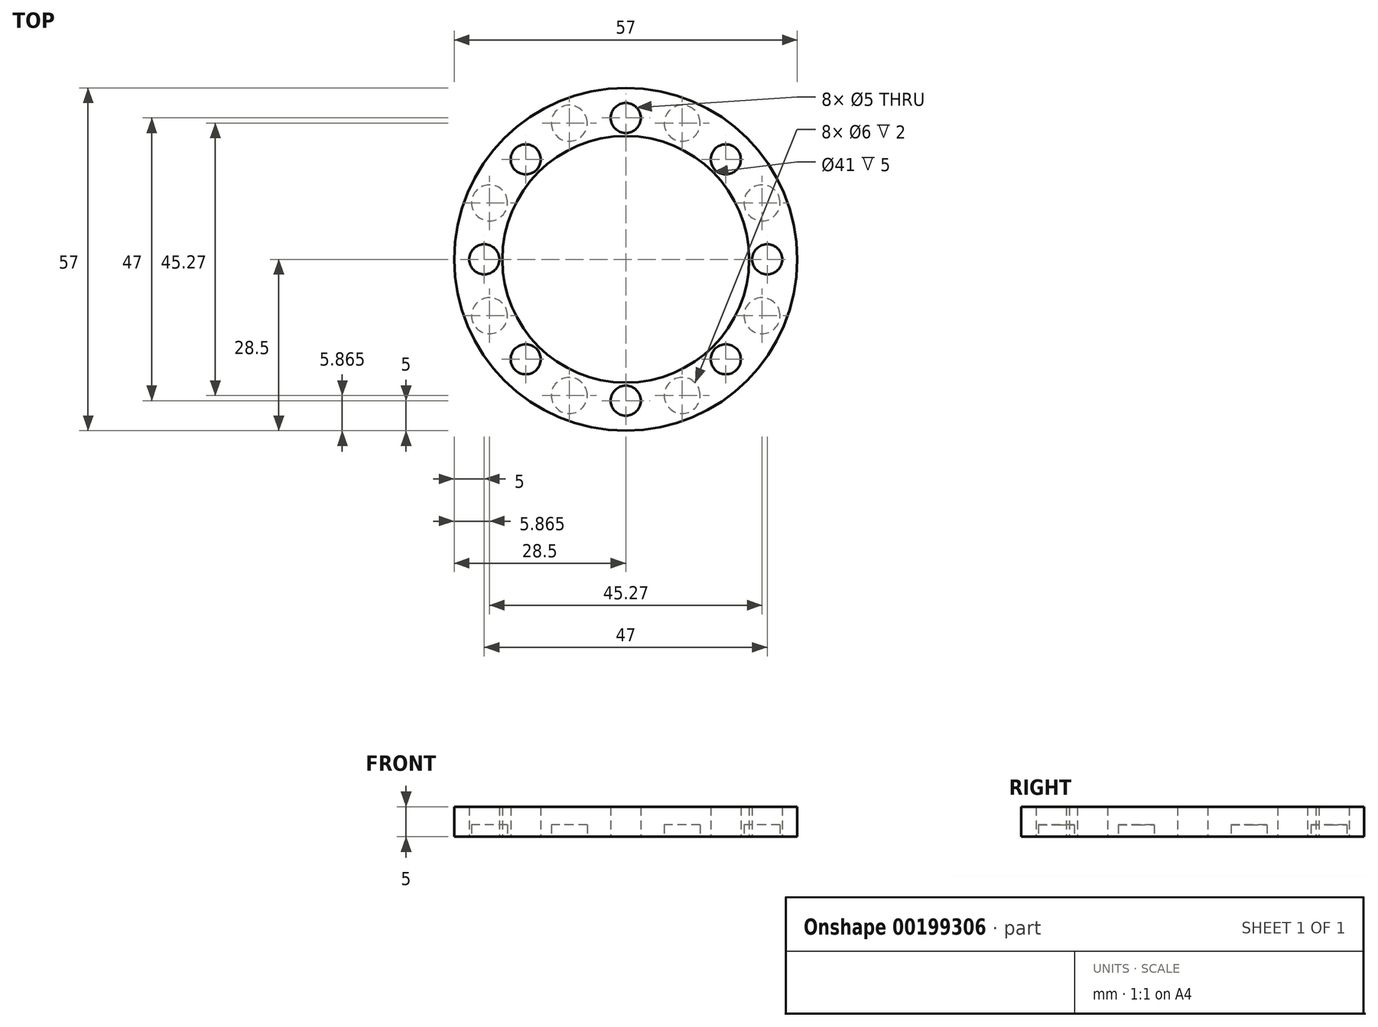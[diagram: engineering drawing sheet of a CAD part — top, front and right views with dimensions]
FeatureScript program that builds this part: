
annotation { "Feature Type Name" : "Feature", "Feature Type Description" : "" }
export const myFeature = defineFeature(function(context is Context, id is Id, definition is map)
    precondition{}
    {
        {
            var Q0;
            Q0=qCreatedBy(makeId("Top.planeOp"),FACE);
            var sketch = newSketch(context, id + "F0", { "sketchPlane" : qUnion([Q0])});
            skCircle(sketch, "E0", {"center": v(0, 0) * mm, "radius": 20.5 * mm});
            skCircle(sketch, "E1.cCircle", {"center": v(0, 0) * mm, "radius": 23.5 * mm, "construction": true});
            skLineSegment(sketch, "E1.0", {"start": v(0, -23.5) * mm, "end": v(-16.62, -16.62) * mm, "construction": true});
            skLineSegment(sketch, "E1.1", {"start": v(-16.62, -16.62) * mm, "end": v(-23.5, 0) * mm, "construction": true});
            skLineSegment(sketch, "E1.2", {"start": v(-23.5, 0) * mm, "end": v(-16.62, 16.62) * mm, "construction": true});
            skLineSegment(sketch, "E1.3", {"start": v(-16.62, 16.62) * mm, "end": v(0, 23.5) * mm, "construction": true});
            skLineSegment(sketch, "E1.4", {"start": v(0, 23.5) * mm, "end": v(16.62, 16.62) * mm, "construction": true});
            skLineSegment(sketch, "E1.5", {"start": v(16.62, 16.62) * mm, "end": v(23.5, 0) * mm, "construction": true});
            skLineSegment(sketch, "E1.6", {"start": v(23.5, 0) * mm, "end": v(16.62, -16.62) * mm, "construction": true});
            skLineSegment(sketch, "E1.7", {"start": v(16.62, -16.62) * mm, "end": v(0, -23.5) * mm, "construction": true});
            skCircle(sketch, "E2.cCircle", {"center": v(0, 0) * mm, "radius": 24.5 * mm, "construction": true});
            skLineSegment(sketch, "E2.0", {"start": v(24.5, 0) * mm, "end": v(22.64, -9.38) * mm, "construction": true});
            skLineSegment(sketch, "E2.1", {"start": v(22.64, -9.38) * mm, "end": v(17.32, -17.32) * mm, "construction": true});
            skLineSegment(sketch, "E2.2", {"start": v(17.32, -17.32) * mm, "end": v(9.38, -22.64) * mm, "construction": true});
            skLineSegment(sketch, "E2.3", {"start": v(9.38, -22.64) * mm, "end": v(0, -24.5) * mm, "construction": true});
            skLineSegment(sketch, "E2.4", {"start": v(0, -24.5) * mm, "end": v(-9.38, -22.64) * mm, "construction": true});
            skLineSegment(sketch, "E2.5", {"start": v(-9.38, -22.64) * mm, "end": v(-17.32, -17.32) * mm, "construction": true});
            skLineSegment(sketch, "E2.6", {"start": v(-17.32, -17.32) * mm, "end": v(-22.64, -9.38) * mm, "construction": true});
            skLineSegment(sketch, "E2.7", {"start": v(-22.64, -9.38) * mm, "end": v(-24.5, 0) * mm, "construction": true});
            skLineSegment(sketch, "E2.8", {"start": v(-24.5, 0) * mm, "end": v(-22.64, 9.38) * mm, "construction": true});
            skLineSegment(sketch, "E2.9", {"start": v(-22.64, 9.38) * mm, "end": v(-17.32, 17.32) * mm, "construction": true});
            skLineSegment(sketch, "E2.10", {"start": v(-17.32, 17.32) * mm, "end": v(-9.38, 22.64) * mm, "construction": true});
            skLineSegment(sketch, "E2.11", {"start": v(-9.38, 22.64) * mm, "end": v(0, 24.5) * mm, "construction": true});
            skLineSegment(sketch, "E2.12", {"start": v(0, 24.5) * mm, "end": v(9.38, 22.64) * mm, "construction": true});
            skLineSegment(sketch, "E2.13", {"start": v(9.38, 22.64) * mm, "end": v(17.32, 17.32) * mm, "construction": true});
            skLineSegment(sketch, "E2.14", {"start": v(17.32, 17.32) * mm, "end": v(22.64, 9.38) * mm, "construction": true});
            skLineSegment(sketch, "E2.15", {"start": v(22.64, 9.38) * mm, "end": v(24.5, 0) * mm, "construction": true});
            skCircle(sketch, "E3", {"center": v(0, 23.5) * mm, "radius": 2.5 * mm});
            skCircle(sketch, "E4", {"center": v(9.38, 22.64) * mm, "radius": 3 * mm});
            skCircle(sketch, "E5.1.0", {"center": v(-16.62, 16.62) * mm, "radius": 2.5 * mm});
            skCircle(sketch, "E5.2.0", {"center": v(-23.5, 0) * mm, "radius": 2.5 * mm});
            skCircle(sketch, "E6.1.3.0", {"center": v(-16.62, -16.62) * mm, "radius": 2.5 * mm});
            skCircle(sketch, "E6.1.4.0", {"center": v(0, -23.5) * mm, "radius": 2.5 * mm});
            skCircle(sketch, "E6.1.5.0", {"center": v(16.62, -16.62) * mm, "radius": 2.5 * mm});
            skCircle(sketch, "E6.1.6.0", {"center": v(23.5, 0) * mm, "radius": 2.5 * mm});
            skCircle(sketch, "E6.1.7.0", {"center": v(16.62, 16.62) * mm, "radius": 2.5 * mm});
            skCircle(sketch, "E7.1.0", {"center": v(-9.38, 22.64) * mm, "radius": 3 * mm});
            skCircle(sketch, "E7.2.0", {"center": v(-22.64, 9.38) * mm, "radius": 3 * mm});
            skCircle(sketch, "E8.1.3.0", {"center": v(-22.64, -9.38) * mm, "radius": 3 * mm});
            skCircle(sketch, "E8.1.4.0", {"center": v(-9.38, -22.64) * mm, "radius": 3 * mm});
            skCircle(sketch, "E8.1.5.0", {"center": v(9.38, -22.64) * mm, "radius": 3 * mm});
            skCircle(sketch, "E8.1.6.0", {"center": v(22.64, -9.38) * mm, "radius": 3 * mm});
            skCircle(sketch, "E8.1.7.0", {"center": v(22.64, 9.38) * mm, "radius": 3 * mm});
            skCircle(sketch, "E9", {"center": v(0, 0) * mm, "radius": 28.5 * mm});
            skSolve(sketch);
        }
        {
            var Q0;
            Q0=makeQuery(id+"F0.imprint","IMPRINT",FACE,{"disambiguationData":[TD([[makeQuery(id+"F0.imprint","IMPRINT",EDGE,{"derivedFrom":sQuery(id+"F0.wireOp",EDGE,"E7.2.0")}),1.0]])]});
            var Q1;
            Q1=makeQuery(id+"F0.imprint","IMPRINT",FACE,{"disambiguationData":[TD([[makeQuery(id+"F0.imprint","IMPRINT",EDGE,{"derivedFrom":sQuery(id+"F0.wireOp",EDGE,"E7.1.0")}),1.0]])]});
            var Q2;
            Q2=makeQuery(id+"F0.imprint","IMPRINT",FACE,{"disambiguationData":[TD([[makeQuery(id+"F0.imprint","IMPRINT",EDGE,{"derivedFrom":sQuery(id+"F0.wireOp",EDGE,"E4")}),1.0]])]});
            var Q3;
            Q3=makeQuery(id+"F0.imprint","IMPRINT",FACE,{"disambiguationData":[TD([[makeQuery(id+"F0.imprint","IMPRINT",EDGE,{"derivedFrom":sQuery(id+"F0.wireOp",EDGE,"E8.1.7.0")}),1.0]])]});
            var Q4;
            Q4=makeQuery(id+"F0.imprint","IMPRINT",FACE,{"disambiguationData":[TD([[makeQuery(id+"F0.imprint","IMPRINT",EDGE,{"derivedFrom":sQuery(id+"F0.wireOp",EDGE,"E8.1.6.0")}),1.0]])]});
            var Q5;
            Q5=makeQuery(id+"F0.imprint","IMPRINT",FACE,{"disambiguationData":[TD([[makeQuery(id+"F0.imprint","IMPRINT",EDGE,{"derivedFrom":sQuery(id+"F0.wireOp",EDGE,"E8.1.5.0")}),1.0]])]});
            var Q6;
            Q6=makeQuery(id+"F0.imprint","IMPRINT",FACE,{"disambiguationData":[TD([[makeQuery(id+"F0.imprint","IMPRINT",EDGE,{"derivedFrom":sQuery(id+"F0.wireOp",EDGE,"E8.1.4.0")}),1.0]])]});
            var Q7;
            Q7=makeQuery(id+"F0.imprint","IMPRINT",FACE,{"disambiguationData":[TD([[makeQuery(id+"F0.imprint","IMPRINT",EDGE,{"derivedFrom":sQuery(id+"F0.wireOp",EDGE,"E8.1.3.0")}),1.0]])]});
            var Q8;
            Q8=makeQuery(id+"F0.imprint","IMPRINT",FACE,{"disambiguationData":[TD([[makeQuery(id+"F0.imprint","IMPRINT",EDGE,{"derivedFrom":sQuery(id+"F0.wireOp",EDGE,"E0")}),-1.0]])]});
            extrude(context, id + "F1", {"entities" : qUnion([Q0, Q1, Q2, Q3, Q4, Q5, Q6, Q7, Q8]), "depth" : 5 * mm});
        }
        {
            var Q0;
            Q0=makeQuery(id+"F0.imprint","IMPRINT",FACE,{"disambiguationData":[TD([[makeQuery(id+"F0.imprint","IMPRINT",EDGE,{"derivedFrom":sQuery(id+"F0.wireOp",EDGE,"E8.1.3.0")}),1.0]])]});
            var Q1;
            Q1=makeQuery(id+"F0.imprint","IMPRINT",FACE,{"disambiguationData":[TD([[makeQuery(id+"F0.imprint","IMPRINT",EDGE,{"derivedFrom":sQuery(id+"F0.wireOp",EDGE,"E8.1.4.0")}),1.0]])]});
            var Q2;
            Q2=makeQuery(id+"F0.imprint","IMPRINT",FACE,{"disambiguationData":[TD([[makeQuery(id+"F0.imprint","IMPRINT",EDGE,{"derivedFrom":sQuery(id+"F0.wireOp",EDGE,"E8.1.5.0")}),1.0]])]});
            var Q3;
            Q3=makeQuery(id+"F0.imprint","IMPRINT",FACE,{"disambiguationData":[TD([[makeQuery(id+"F0.imprint","IMPRINT",EDGE,{"derivedFrom":sQuery(id+"F0.wireOp",EDGE,"E8.1.6.0")}),1.0]])]});
            var Q4;
            Q4=makeQuery(id+"F0.imprint","IMPRINT",FACE,{"disambiguationData":[TD([[makeQuery(id+"F0.imprint","IMPRINT",EDGE,{"derivedFrom":sQuery(id+"F0.wireOp",EDGE,"E8.1.7.0")}),1.0]])]});
            var Q5;
            Q5=makeQuery(id+"F0.imprint","IMPRINT",FACE,{"disambiguationData":[TD([[makeQuery(id+"F0.imprint","IMPRINT",EDGE,{"derivedFrom":sQuery(id+"F0.wireOp",EDGE,"E4")}),1.0]])]});
            var Q6;
            Q6=makeQuery(id+"F0.imprint","IMPRINT",FACE,{"disambiguationData":[TD([[makeQuery(id+"F0.imprint","IMPRINT",EDGE,{"derivedFrom":sQuery(id+"F0.wireOp",EDGE,"E7.1.0")}),1.0]])]});
            var Q7;
            Q7=makeQuery(id+"F0.imprint","IMPRINT",FACE,{"disambiguationData":[TD([[makeQuery(id+"F0.imprint","IMPRINT",EDGE,{"derivedFrom":sQuery(id+"F0.wireOp",EDGE,"E7.2.0")}),1.0]])]});
            extrude(context, id + "F2", {"entities" : qUnion([Q0, Q1, Q2, Q3, Q4, Q5, Q6, Q7]), "operationType" : NewBodyOperationType.REMOVE, "depth" : 2 * mm});
        }
    });
